# Revit family: ElectricalFixture_Hager_IP66WallSwitches
name_source: partatom
category: Lighting Fixtures
revit_build: Autodesk Revit 2015 (Build: 20160512_1515(x64)
units: mm (PartAtom-declared; Revit-internal decimal feet)

## types (4) — shared parameters
AssetType = Fixed
Back Plate Depth = 39 mm
Back Plate Height = 90 mm
Back Plate Width = 90 mm
Category = ElectricalFixture
ClassificationName = Uniclass2015
ClassificationValue = Pr_65_72_97
Colour = RAL9010WhiteGloss
Default Elevation = 500 mm
DocumentationCertificates = http://www.hager.co.uk
DocumentationLiterature = http://www.hager.co.uk
DocumentationTechnical = http://www.hager.co.uk
DurationUnit = Years
ExpectedLife = 25
Extrusion From Wall = 17 mm
Frequency = 50/60Hz
IfcExportAs = ElectricalFixture
IfcExportType = ElectricalFixture
Keynote = 16400
Manufacturer = Hager
ManufacturerName = Hager
Material = Urea Formaldehyde Thermoset Plastic
NBSDescription = ElectricalFixture
NBSReference = Pr_65_72_97
NominalDepth = 55 mm
NominalHeight = 90 mm
NominalLength = 90 mm
NominalWidth = 64 mm
Shape = Rectangular
Supply Phase = 1
Switch = Yes
URL = http://www.hager.co.uk
Voltage = 230V/240V
WarrantyDescription = See Manufacturer
WarrantyDurationParts = 10
WarrantyDurationUnit = Years
WarrantyGuarantorParts = 10
_BimstoreBibleVersion = V14
_DistributedBy = www.bimstore.co.uk
zero-valued in all types: ReplacementCost, ServiceLifeDuration, Switch Height, Switch Width, WarrantyDurationLabor, _BimSpecGuid, _CurrentRevision

## per-type parameters (varying)
| type | 1Gang | 2 Gang | BIMObjectName | Description | EAN | Features | LED Indicator Switch | NBSObjectName | One Way | Two Way | TypeName |
| WXPPS12 | Yes | No | Hager_ElectricalFixture_WXPPS12 | IP6610AX1Gang2WaySwitch | 3250617260039 | IP6610AX1Gang2WaySwitch | No | Hager_IP66WallSwitches_WXPPS12 | No | Yes | ElectricalFixture_IP66WallSwitches_WXPPS12 |
| WXPPS22 | No | Yes | Hager_ElectricalFixture_WXPPS22 | IP6610AX2Gang2WaySwitch | 3250617260053 | IP6610AX2Gang2WaySwitch | No | Hager_IP66WallSwitches_WXPPS22 | No | Yes | ElectricalFixture_IP66WallSwitches_WXPPS12 |
| WXPPS12B | Yes | No | Hager_ElectricalFixture_WXPPS12B | IP6610AX1GangPressBellSwitch | 3250617260039 | IP6610AX1GangPressBellSwitch | No | Hager_IP66WallSwitches_WXPPS12B | No | Yes | ElectricalFixture_IP66WallSwitches_WXPPS12B |
| WXPDP84 | Yes | No | Hager_ElectricalFixture_WXPDP84 | IP6620A1Gang1WayDoublePoleSwitch | 3250617260008 | IP6620A1Gang1WayDoublePoleSwitch | Yes | Hager_IP66WallSwitches_WXPDP84 | Yes | No | ElectricalFixture_IP66WallSwitches_WXPDP84 |

note: column(s) folded — value = type name in every type: Model, ModelNumber, ModelReference, Type Comments

## geometry (parser evidence)
native form markers: Blend x8, Sweep x3
no freeform markers — native parametric forms only
